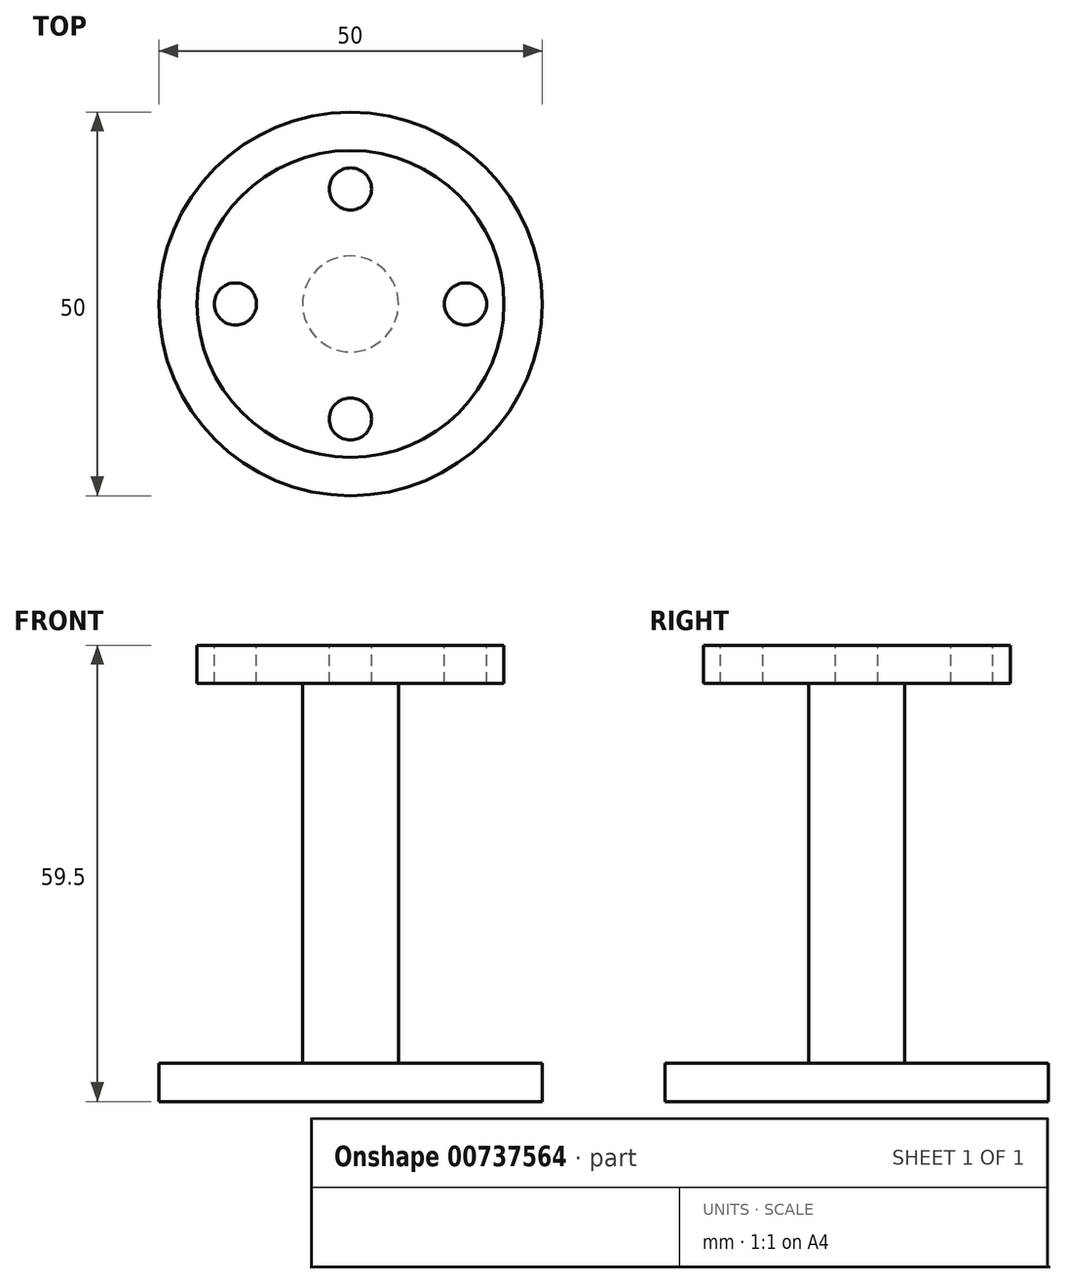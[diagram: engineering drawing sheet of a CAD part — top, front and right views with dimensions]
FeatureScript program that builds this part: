
annotation { "Feature Type Name" : "Feature", "Feature Type Description" : "" }
export const myFeature = defineFeature(function(context is Context, id is Id, definition is map)
    precondition{}
    {
        {
            var Q0;
            Q0=qCreatedBy(makeId("Top.planeOp"),FACE);
            var sketch = newSketch(context, id + "F0", { "sketchPlane" : qUnion([Q0])});
            skCircle(sketch, "E0", {"center": v(0, 0) * mm, "radius": 25 * mm});
            skSolve(sketch);
        }
        {
            var Q0;
            Q0 = qSketchRegion(id + "F0", true);
            extrude(context, id + "F1", {"entities" : qUnion([Q0]), "depth" : 5 * mm, "offsetDistance" : 25.4 * mm});
        }
        {
            var Q0;
            Q0=makeQuery(id+"F1.opExtrude","CAP_FACE",FACE,{"disambiguationData":[OSD([sQuery(id+"F0.wireOp",EDGE,"E0")])],"isStart":false});
            var sketch = newSketch(context, id + "F2", { "sketchPlane" : qUnion([Q0])});
            skCircle(sketch, "E1", {"center": v(0, 0) * mm, "radius": 6.25 * mm});
            skSolve(sketch);
        }
        {
            var Q0;
            Q0 = qSketchRegion(id + "F2", true);
            extrude(context, id + "F3", {"entities" : qUnion([Q0]), "operationType" : NewBodyOperationType.ADD, "depth" : 49.5 * mm, "offsetDistance" : 25.4 * mm});
        }
        {
            var Q0;
            Q0=makeQuery(id+"F3.opExtrude","CAP_FACE",FACE,{"disambiguationData":[OSD([sQuery(id+"F2.wireOp",EDGE,"E1")])],"isStart":false});
            var sketch = newSketch(context, id + "F4", { "sketchPlane" : qUnion([Q0])});
            skCircle(sketch, "E2", {"center": v(0, 0) * mm, "radius": 20 * mm});
            skSolve(sketch);
        }
        {
            var Q0;
            Q0 = qSketchRegion(id + "F4", true);
            extrude(context, id + "F5", {"entities" : qUnion([Q0]), "operationType" : NewBodyOperationType.ADD, "depth" : 5 * mm, "offsetDistance" : 25.4 * mm});
        }
        {
            var Q0;
            Q0=makeQuery(id+"F5.opExtrude","CAP_FACE",FACE,{"disambiguationData":[OSD([sQuery(id+"F4.wireOp",EDGE,"E2")])],"isStart":false});
            var sketch = newSketch(context, id + "F6", { "sketchPlane" : qUnion([Q0])});
            skCircle(sketch, "E3", {"center": v(15, 0) * mm, "radius": 2.75 * mm});
            skCircle(sketch, "E4.1.0", {"center": v(0, 15) * mm, "radius": 2.75 * mm});
            skCircle(sketch, "E4.2.0", {"center": v(-15, 0) * mm, "radius": 2.75 * mm});
            skCircle(sketch, "E4.3.0", {"center": v(0, -15) * mm, "radius": 2.75 * mm});
            skPoint(sketch, "E4.center", {"position": v(0, 0) * mm});
            skSolve(sketch);
        }
        {
            var Q0;
            Q0=makeQuery(id+"F6.imprint","IMPRINT",FACE,{"disambiguationData":[TD([[makeQuery(id+"F6.imprint","IMPRINT",EDGE,{"derivedFrom":sQuery(id+"F6.wireOp",EDGE,"E4.1.0")}),1.0]])]});
            var Q1;
            Q1=makeQuery(id+"F6.imprint","IMPRINT",FACE,{"disambiguationData":[TD([[makeQuery(id+"F6.imprint","IMPRINT",EDGE,{"derivedFrom":sQuery(id+"F6.wireOp",EDGE,"E3")}),1.0]])]});
            var Q2;
            Q2=makeQuery(id+"F6.imprint","IMPRINT",FACE,{"disambiguationData":[TD([[makeQuery(id+"F6.imprint","IMPRINT",EDGE,{"derivedFrom":sQuery(id+"F6.wireOp",EDGE,"E4.3.0")}),1.0]])]});
            var Q3;
            Q3=makeQuery(id+"F6.imprint","IMPRINT",FACE,{"disambiguationData":[TD([[makeQuery(id+"F6.imprint","IMPRINT",EDGE,{"derivedFrom":sQuery(id+"F6.wireOp",EDGE,"E4.2.0")}),1.0]])]});
            extrude(context, id + "F7", {"entities" : qUnion([Q0, Q1, Q2, Q3]), "operationType" : NewBodyOperationType.REMOVE, "oppositeDirection" : true, "depth" : 5 * mm, "offsetDistance" : 25.4 * mm});
        }
    });
